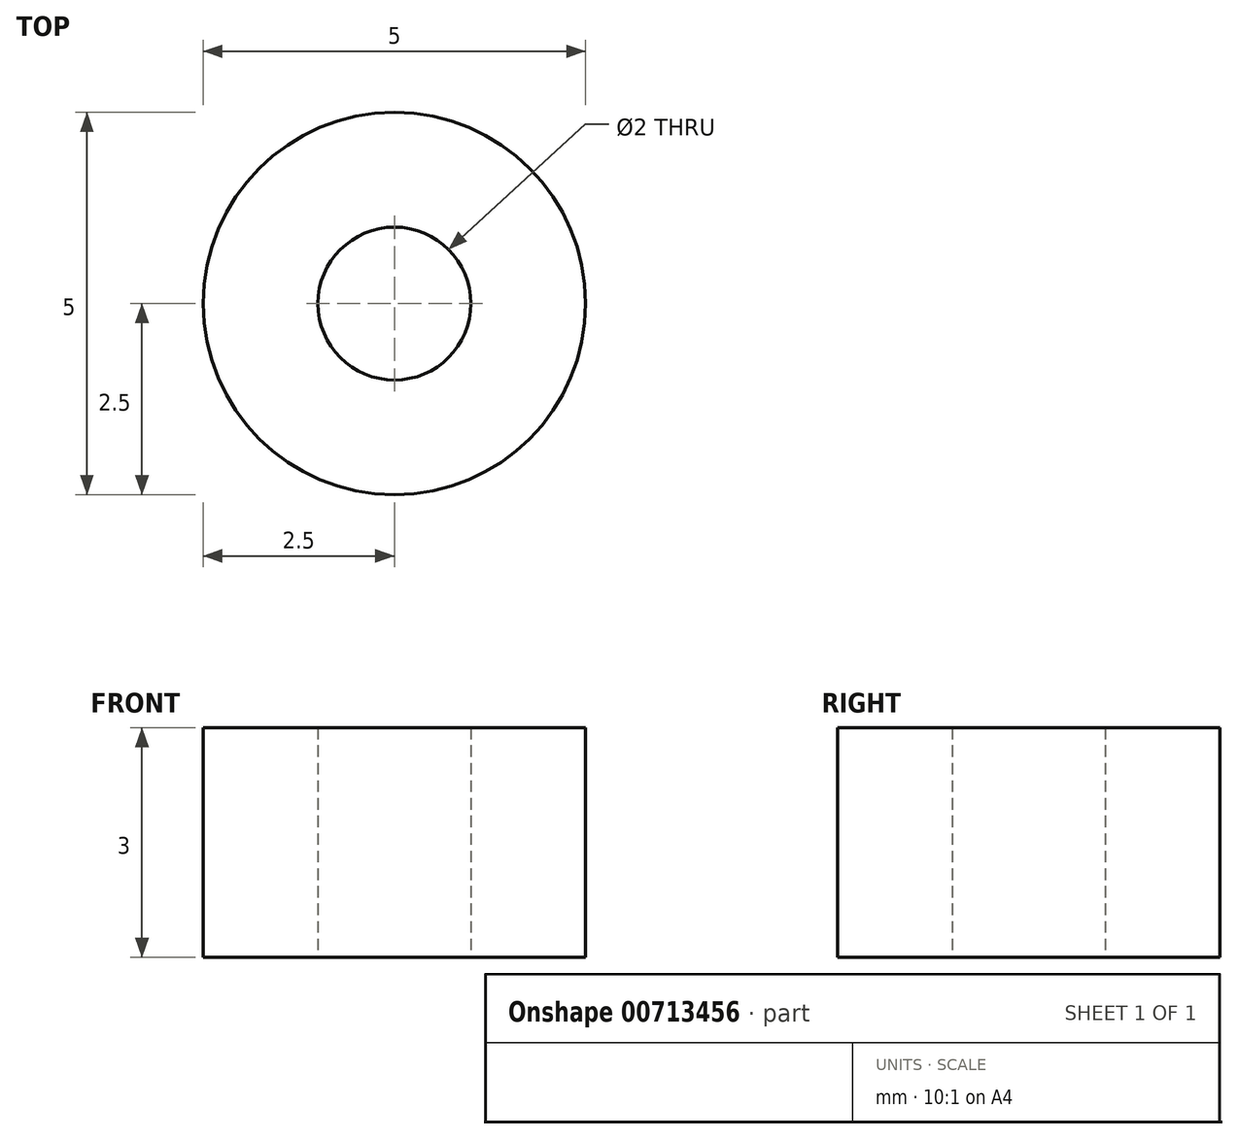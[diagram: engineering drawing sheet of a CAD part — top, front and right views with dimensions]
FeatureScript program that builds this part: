
annotation { "Feature Type Name" : "Feature", "Feature Type Description" : "" }
export const myFeature = defineFeature(function(context is Context, id is Id, definition is map)
    precondition{}
    {
        {
            var Q0;
            Q0=qCreatedBy(makeId("Top.planeOp"),FACE);
            var sketch = newSketch(context, id + "F0", { "sketchPlane" : qUnion([Q0])});
            skCircle(sketch, "E0", {"center": v(0, 0) * mm, "radius": 2.5 * mm});
            skCircle(sketch, "E1", {"center": v(0, 0) * mm, "radius": 1 * mm});
            skSolve(sketch);
        }
        {
            var Q0;
            Q0 = qSketchRegion(id + "F0", true);
            extrude(context, id + "F1", {"entities" : qUnion([Q0]), "depth" : 3 * mm, "offsetDistance" : 25 * mm});
        }
    });
